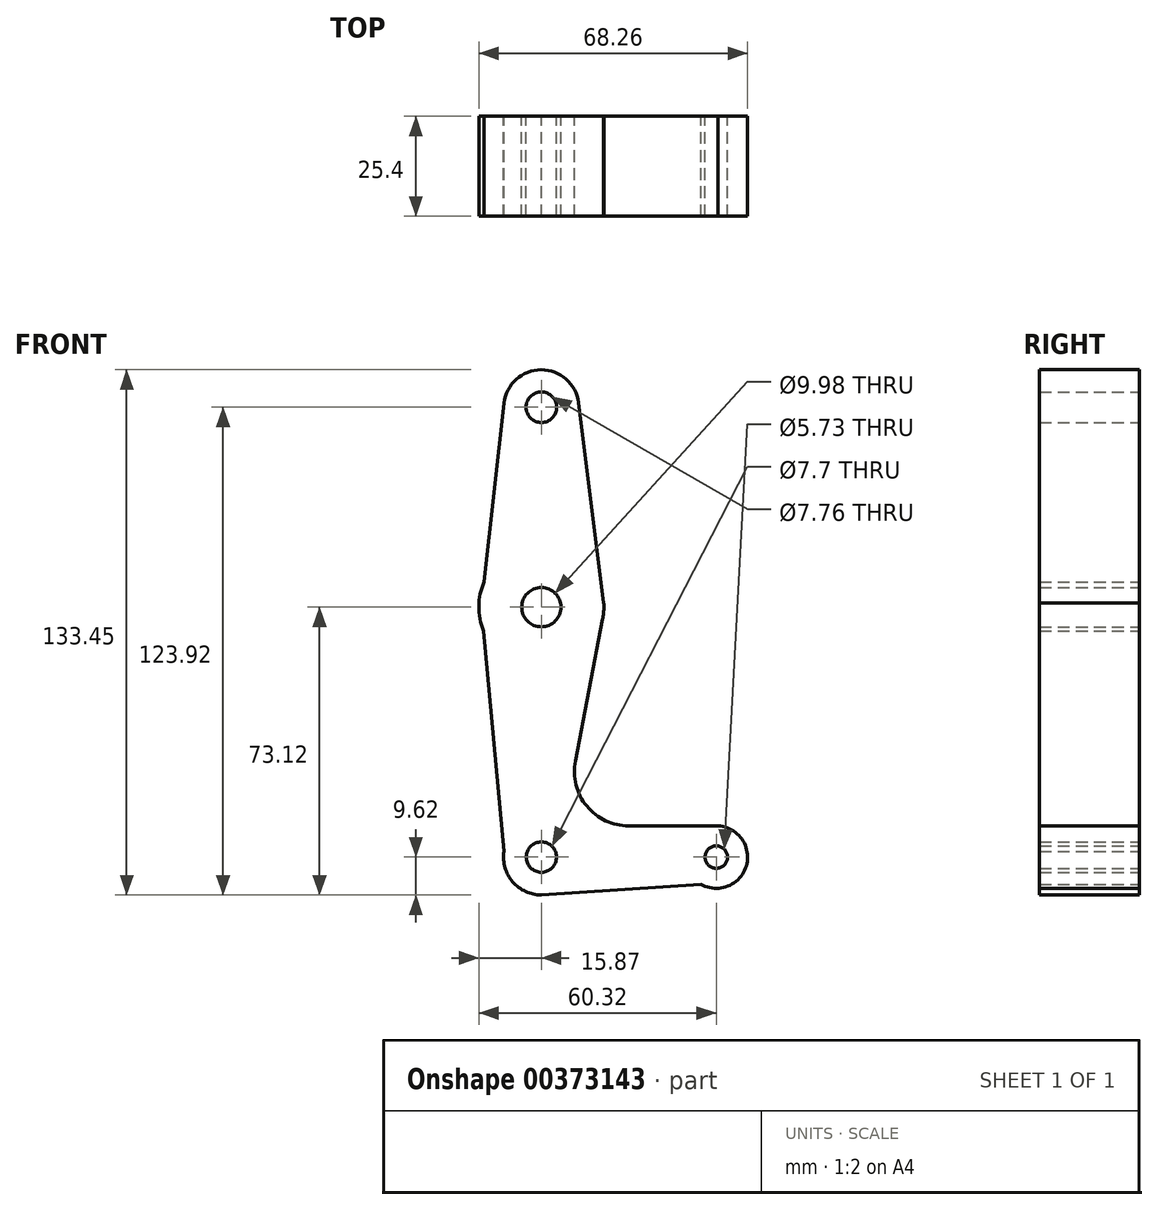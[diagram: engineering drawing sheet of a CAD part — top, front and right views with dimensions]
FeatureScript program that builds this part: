
annotation { "Feature Type Name" : "Feature", "Feature Type Description" : "" }
export const myFeature = defineFeature(function(context is Context, id is Id, definition is map)
    precondition{}
    {
        {
            var Q0;
            Q0=qCreatedBy(makeId("Front.planeOp"),FACE);
            var sketch = newSketch(context, id + "F0", { "sketchPlane" : qUnion([Q0])});
            skLineSegment(sketch, "E0", {"start": v(0, 0) * mm, "end": v(0, 114.3) * mm});
            skLineSegment(sketch, "E1", {"start": v(0, 0) * mm, "end": v(44.45, 0) * mm});
            skCircle(sketch, "E2", {"center": v(0, 0) * mm, "radius": 9.62 * mm});
            skCircle(sketch, "E3", {"center": v(44.45, 0) * mm, "radius": 7.94 * mm});
            skCircle(sketch, "E4", {"center": v(0, 114.3) * mm, "radius": 9.53 * mm});
            skCircle(sketch, "E5", {"center": v(0, 63.5) * mm, "radius": 15.88 * mm});
            skLineSegment(sketch, "E6", {"start": v(-9.47, 115.36) * mm, "end": v(-15.58, 60.48) * mm});
            skLineSegment(sketch, "E7", {"start": v(-14.7, 57.5) * mm, "end": v(-9.1, -3.11) * mm});
            skLineSegment(sketch, "E8", {"start": v(0, -9.62) * mm, "end": v(40.52, -6.9) * mm});
            skLineSegment(sketch, "E9", {"start": v(44.9, 7.92) * mm, "end": v(22.2, 7.92) * mm});
            skLineSegment(sketch, "E10", {"start": v(8.62, 24.38) * mm, "end": v(15.59, 60.5) * mm});
            skLineSegment(sketch, "E11", {"start": v(15.84, 64.5) * mm, "end": v(9.45, 115.49) * mm});
            skCircle(sketch, "E12", {"center": v(0, 114.3) * mm, "radius": 3.88 * mm});
            skCircle(sketch, "E13", {"center": v(0, 63.5) * mm, "radius": 5 * mm});
            skCircle(sketch, "E14", {"center": v(0, 0) * mm, "radius": 3.85 * mm});
            skCircle(sketch, "E15", {"center": v(44.45, 0) * mm, "radius": 2.86 * mm});
            skPoint(sketch, "E16.visualSharp", {"position": v(5.45, 7.92) * mm});
            skArc(sketch, "E16.filletArc", {"start": v(8.62, 24.38) * mm, "mid": v(11.54, 12.95) * mm, "end": v(22.2, 7.92) * mm});
            skSolve(sketch);
        }
        {
            var Q0;
            {var subQ0=sQuery(id+"F0.wireOp",EDGE,"E7");var subQ1=sQuery(id+"F0.wireOp",EDGE,"E2");var subQ2=makeQuery(id+"F0.imprint","INTERSECT",VERTEX,{"disambiguationData":[OD(0.0)],"derivedFrom":[subQ1,subQ0]});Q0=makeQuery(id+"F0.imprint","IMPRINT",FACE,{"disambiguationData":[TD([[makeQuery(id+"F0.imprint","IMPRINT",EDGE,{"disambiguationData":[TD([[subQ2,1.0]])],"derivedFrom":subQ1}),1.0]])]});}
            var Q1;
            {var subQ0=sQuery(id+"F0.wireOp",EDGE,"E8");var subQ1=sQuery(id+"F0.wireOp",EDGE,"E2");var subQ2=makeQuery(id+"F0.imprint","INTERSECT",VERTEX,{"disambiguationData":[OD(0.0)],"derivedFrom":[subQ1,subQ0]});Q1=makeQuery(id+"F0.imprint","IMPRINT",FACE,{"disambiguationData":[TD([[makeQuery(id+"F0.imprint","IMPRINT",EDGE,{"disambiguationData":[TD([[subQ2,-1.0]])],"derivedFrom":subQ1}),1.0]])]});}
            var Q2;
            {var subQ0=sQuery(id+"F0.wireOp",EDGE,"E9");var subQ1=sQuery(id+"F0.wireOp",EDGE,"E3");var subQ2=makeQuery(id+"F0.imprint","INTERSECT",VERTEX,{"disambiguationData":[OD(0.0)],"derivedFrom":[subQ1,subQ0]});Q2=makeQuery(id+"F0.imprint","IMPRINT",FACE,{"disambiguationData":[TD([[makeQuery(id+"F0.imprint","IMPRINT",EDGE,{"disambiguationData":[TD([[subQ2,-1.0]])],"derivedFrom":subQ1}),1.0]])]});}
            var Q3;
            {var subQ0=sQuery(id+"F0.wireOp",EDGE,"E11");var subQ1=sQuery(id+"F0.wireOp",EDGE,"E5");var subQ2=makeQuery(id+"F0.imprint","INTERSECT",VERTEX,{"disambiguationData":[OD(0.0)],"derivedFrom":[subQ1,subQ0]});Q3=makeQuery(id+"F0.imprint","IMPRINT",FACE,{"disambiguationData":[TD([[makeQuery(id+"F0.imprint","IMPRINT",EDGE,{"disambiguationData":[TD([[subQ2,-1.0]])],"derivedFrom":subQ1}),1.0]])]});}
            var Q4;
            {var subQ0=sQuery(id+"F0.wireOp",EDGE,"E6");var subQ1=sQuery(id+"F0.wireOp",EDGE,"E5");var subQ2=makeQuery(id+"F0.imprint","INTERSECT",VERTEX,{"disambiguationData":[OD(0.0)],"derivedFrom":[subQ1,subQ0]});Q4=makeQuery(id+"F0.imprint","IMPRINT",FACE,{"disambiguationData":[TD([[makeQuery(id+"F0.imprint","IMPRINT",EDGE,{"disambiguationData":[TD([[subQ2,1.0]])],"derivedFrom":subQ1}),1.0]])]});}
            var Q5;
            {var subQ0=sQuery(id+"F0.wireOp",EDGE,"E2");var subQ1=sQuery(id+"F0.wireOp",EDGE,"E0");var subQ2=makeQuery(id+"F0.imprint","INTERSECT",VERTEX,{"derivedFrom":[subQ1,subQ0]});Q5=makeQuery(id+"F0.imprint","IMPRINT",FACE,{"disambiguationData":[TD([[makeQuery(id+"F0.imprint","IMPRINT",EDGE,{"disambiguationData":[TD([[subQ2,-1.0]])],"derivedFrom":subQ1}),1.0]])]});}
            var Q6;
            {var subQ0=sQuery(id+"F0.wireOp",EDGE,"E4");var subQ1=sQuery(id+"F0.wireOp",EDGE,"E0");var subQ2=makeQuery(id+"F0.imprint","INTERSECT",VERTEX,{"derivedFrom":[subQ1,subQ0]});Q6=makeQuery(id+"F0.imprint","IMPRINT",FACE,{"disambiguationData":[TD([[makeQuery(id+"F0.imprint","IMPRINT",EDGE,{"disambiguationData":[TD([[subQ2,1.0]])],"derivedFrom":subQ1}),1.0]])]});}
            var Q7;
            {var subQ0=sQuery(id+"F0.wireOp",EDGE,"E4");var subQ1=sQuery(id+"F0.wireOp",EDGE,"E0");var subQ2=makeQuery(id+"F0.imprint","INTERSECT",VERTEX,{"derivedFrom":[subQ1,subQ0]});Q7=makeQuery(id+"F0.imprint","IMPRINT",FACE,{"disambiguationData":[TD([[makeQuery(id+"F0.imprint","IMPRINT",EDGE,{"disambiguationData":[TD([[subQ2,1.0]])],"derivedFrom":subQ1}),-1.0]])]});}
            var Q8;
            {var subQ0=sQuery(id+"F0.wireOp",EDGE,"E3");var subQ1=sQuery(id+"F0.wireOp",EDGE,"E1");var subQ2=makeQuery(id+"F0.imprint","INTERSECT",VERTEX,{"derivedFrom":[subQ1,subQ0]});Q8=makeQuery(id+"F0.imprint","IMPRINT",FACE,{"disambiguationData":[TD([[makeQuery(id+"F0.imprint","IMPRINT",EDGE,{"disambiguationData":[TD([[subQ2,1.0]])],"derivedFrom":subQ1}),-1.0]])]});}
            var Q9;
            Q9=makeQuery(id+"F0.imprint","IMPRINT",FACE,{"disambiguationData":[TD([[makeQuery(id+"F0.imprint","IMPRINT",EDGE,{"derivedFrom":sQuery(id+"F0.wireOp",EDGE,"E12")}),-1.0]])]});
            var Q10;
            Q10=makeQuery(id+"F0.imprint","IMPRINT",FACE,{"disambiguationData":[TD([[makeQuery(id+"F0.imprint","IMPRINT",EDGE,{"derivedFrom":sQuery(id+"F0.wireOp",EDGE,"E15")}),-1.0]])]});
            var Q11;
            {var subQ0=sQuery(id+"F0.wireOp",EDGE,"E5");var subQ2=sQuery(id+"F0.wireOp",EDGE,"E0");var subQ3=makeQuery(id+"F0.imprint","INTERSECT",VERTEX,{"disambiguationData":[OD(0.0)],"derivedFrom":[subQ2,subQ0]});Q11=makeQuery(id+"F0.imprint","IMPRINT",FACE,{"disambiguationData":[TD([[makeQuery(id+"F0.imprint","IMPRINT",EDGE,{"disambiguationData":[TD([[subQ3,-1.0]])],"derivedFrom":subQ2}),-1.0]])]});}
            var Q12;
            {var subQ1=sQuery(id+"F0.wireOp",EDGE,"E5");var subQ5=sQuery(id+"F0.wireOp",EDGE,"E0");var subQ9=makeQuery(id+"F0.imprint","INTERSECT",VERTEX,{"disambiguationData":[OD(0.0)],"derivedFrom":[subQ5,subQ1]});Q12=makeQuery(id+"F0.imprint","IMPRINT",FACE,{"disambiguationData":[TD([[makeQuery(id+"F0.imprint","IMPRINT",EDGE,{"disambiguationData":[TD([[subQ9,-1.0]])],"derivedFrom":subQ5}),1.0]])]});}
            var Q13;
            {var subQ6=sQuery(id+"F0.wireOp",EDGE,"E14");var subQ7=sQuery(id+"F0.wireOp",EDGE,"E0");var subQ8=makeQuery(id+"F0.imprint","INTERSECT",VERTEX,{"derivedFrom":[subQ7,subQ6]});Q13=makeQuery(id+"F0.imprint","IMPRINT",FACE,{"disambiguationData":[TD([[makeQuery(id+"F0.imprint","IMPRINT",EDGE,{"disambiguationData":[TD([[subQ8,-1.0]])],"derivedFrom":subQ7}),1.0]])]});}
            var Q14;
            {var subQ9=sQuery(id+"F0.wireOp",EDGE,"E10");Q14=makeQuery(id+"F0.imprint","IMPRINT",FACE,{"disambiguationData":[TD([[makeQuery(id+"F0.imprint","IMPRINT",EDGE,{"derivedFrom":subQ9}),1.0]])]});}
            var Q15;
            {var subQ0=sQuery(id+"F0.wireOp",EDGE,"E14");var subQ1=sQuery(id+"F0.wireOp",EDGE,"E0");var subQ2=makeQuery(id+"F0.imprint","INTERSECT",VERTEX,{"derivedFrom":[subQ1,subQ0]});Q15=makeQuery(id+"F0.imprint","IMPRINT",FACE,{"disambiguationData":[TD([[makeQuery(id+"F0.imprint","IMPRINT",EDGE,{"disambiguationData":[TD([[subQ2,-1.0]])],"derivedFrom":subQ1}),-1.0]])]});}
            extrude(context, id + "F1", {"entities" : qUnion([Q0, Q1, Q2, Q3, Q4, Q5, Q6, Q7, Q8, Q9, Q10, Q11, Q12, Q13, Q14, Q15]), "depth" : 25.4 * mm});
        }
    });
